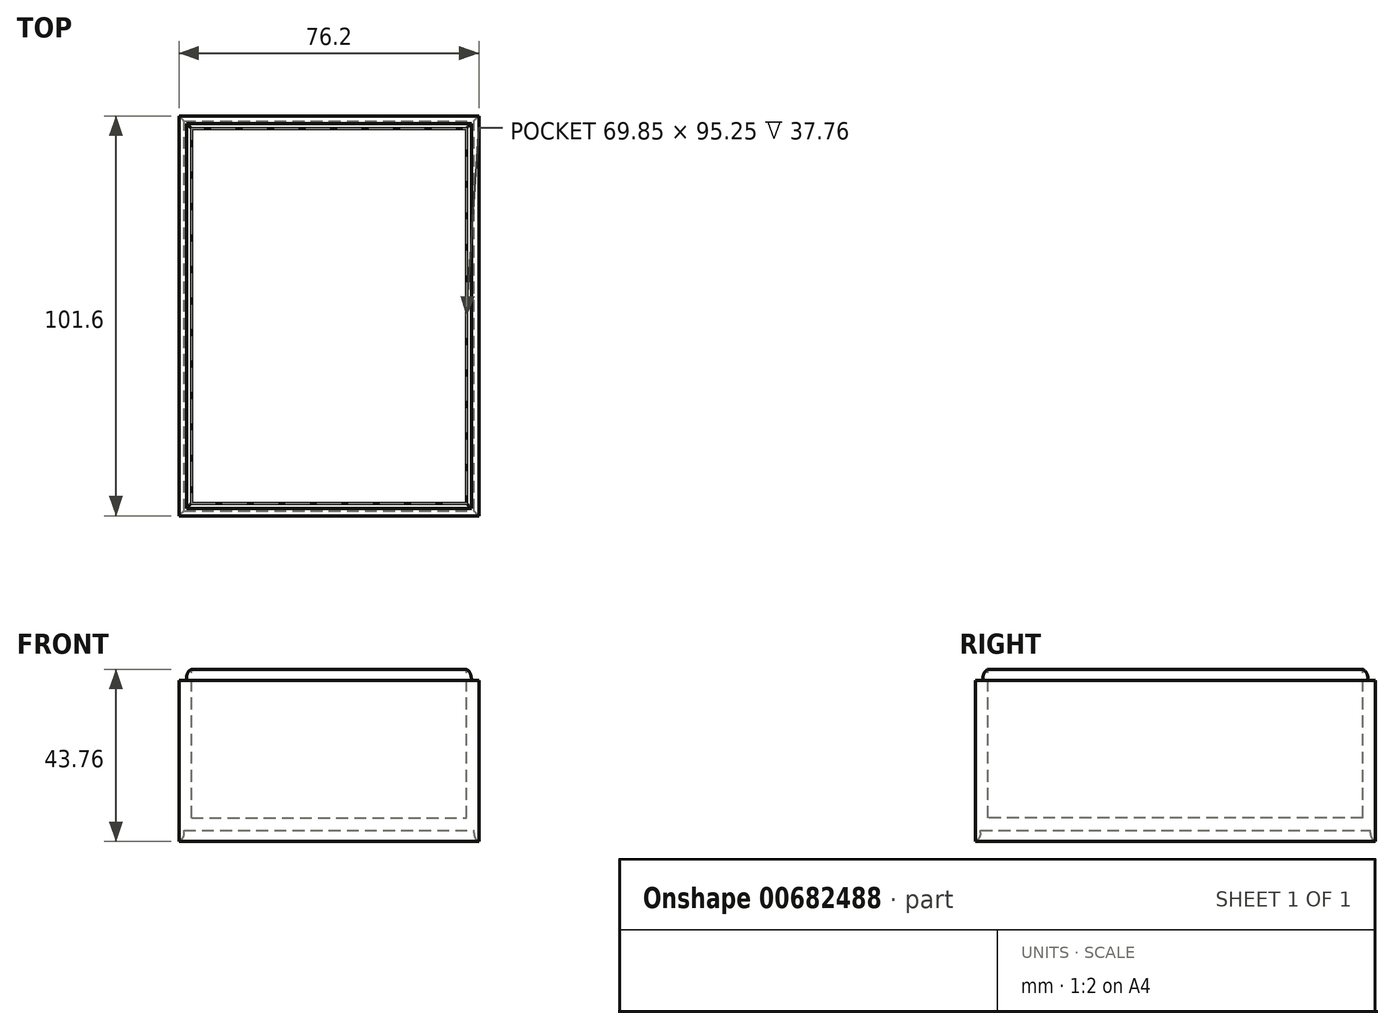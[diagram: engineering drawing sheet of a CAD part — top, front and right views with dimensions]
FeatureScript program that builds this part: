
annotation { "Feature Type Name" : "Feature", "Feature Type Description" : "" }
export const myFeature = defineFeature(function(context is Context, id is Id, definition is map)
    precondition{}
    {
        {
            var Q0;
            Q0=qCreatedBy(makeId("Top.planeOp"),FACE);
            var sketch = newSketch(context, id + "F0", { "sketchPlane" : qUnion([Q0])});
            skLineSegment(sketch, "E0.bottom", {"start": v(38.1, 50.8) * mm, "end": v(-38.1, 50.8) * mm});
            skLineSegment(sketch, "E0.top", {"start": v(38.1, -50.8) * mm, "end": v(-38.1, -50.8) * mm});
            skLineSegment(sketch, "E0.left", {"start": v(38.1, 50.8) * mm, "end": v(38.1, -50.8) * mm});
            skLineSegment(sketch, "E0.right", {"start": v(-38.1, 50.8) * mm, "end": v(-38.1, -50.8) * mm});
            skPoint(sketch, "E0.middle", {"position": v(0, 0) * mm});
            skSolve(sketch);
        }
        {
            var Q0;
            Q0 = qSketchRegion(id + "F0", true);
            extrude(context, id + "F1", {"entities" : qUnion([Q0]), "depth" : 38.1 * mm, "offsetDistance" : 25.4 * mm});
        }
        {
            var Q0;
            Q0=makeQuery(id+"F1.opExtrude","CAP_FACE",FACE,{"disambiguationData":[OSD([sQuery(id+"F0.wireOp",EDGE,"E0.bottom"),sQuery(id+"F0.wireOp",EDGE,"E0.top"),sQuery(id+"F0.wireOp",EDGE,"E0.left"),sQuery(id+"F0.wireOp",EDGE,"E0.right")])],"isStart":false});
            var sketch = newSketch(context, id + "F2", { "sketchPlane" : qUnion([Q0])});
            skLineSegment(sketch, "E1.bottom", {"start": v(-34.92, 47.63) * mm, "end": v(34.92, 47.63) * mm});
            skLineSegment(sketch, "E1.top", {"start": v(-34.92, -47.63) * mm, "end": v(34.92, -47.63) * mm});
            skLineSegment(sketch, "E1.left", {"start": v(-34.92, 47.63) * mm, "end": v(-34.92, -47.63) * mm});
            skLineSegment(sketch, "E1.right", {"start": v(34.92, 47.63) * mm, "end": v(34.92, -47.63) * mm});
            skPoint(sketch, "E1.middle", {"position": v(0, 0) * mm});
            skSolve(sketch);
        }
        {
            var Q0;
            Q0 = qSketchRegion(id + "F2", true);
            extrude(context, id + "F3", {"entities" : qUnion([Q0]), "operationType" : NewBodyOperationType.REMOVE, "oppositeDirection" : true, "depth" : 34.92 * mm, "offsetDistance" : 25.4 * mm});
        }
        {
            var Q0;
            Q0=makeQuery(id+"F1.opExtrude","CAP_FACE",FACE,{"disambiguationData":[OSD([sQuery(id+"F0.wireOp",EDGE,"E0.bottom"),sQuery(id+"F0.wireOp",EDGE,"E0.top"),sQuery(id+"F0.wireOp",EDGE,"E0.left"),sQuery(id+"F0.wireOp",EDGE,"E0.right")])],"isStart":false});
            var sketch = newSketch(context, id + "F4", { "sketchPlane" : qUnion([Q0])});
            skLineSegment(sketch, "E2.bottom", {"start": v(-36.2, 48.9) * mm, "end": v(36.2, 48.9) * mm});
            skLineSegment(sketch, "E2.top", {"start": v(-36.2, -48.9) * mm, "end": v(36.2, -48.9) * mm});
            skLineSegment(sketch, "E2.left", {"start": v(-36.2, 48.9) * mm, "end": v(-36.2, -48.9) * mm});
            skLineSegment(sketch, "E2.right", {"start": v(36.2, 48.9) * mm, "end": v(36.2, -48.9) * mm});
            skPoint(sketch, "E2.middle", {"position": v(0, 0) * mm});
            skLineSegment(sketch, "E3.bottom", {"start": v(-34.92, 47.63) * mm, "end": v(34.92, 47.63) * mm});
            skLineSegment(sketch, "E3.top", {"start": v(-34.92, -47.63) * mm, "end": v(34.92, -47.63) * mm});
            skLineSegment(sketch, "E3.left", {"start": v(-34.92, 47.63) * mm, "end": v(-34.92, -47.63) * mm});
            skLineSegment(sketch, "E3.right", {"start": v(34.92, 47.63) * mm, "end": v(34.92, -47.63) * mm});
            skSolve(sketch);
        }
        {
            var Q0;
            Q0 = qSketchRegion(id + "F4", true);
            extrude(context, id + "F5", {"entities" : qUnion([Q0]), "operationType" : NewBodyOperationType.ADD, "depth" : 3.17 * mm, "offsetDistance" : 25.4 * mm});
        }
        {
            var Q0;
            Q0=makeQuery(id+"F1.opExtrude","CAP_FACE",FACE,{"disambiguationData":[OSD([sQuery(id+"F0.wireOp",EDGE,"E0.bottom"),sQuery(id+"F0.wireOp",EDGE,"E0.top"),sQuery(id+"F0.wireOp",EDGE,"E0.left"),sQuery(id+"F0.wireOp",EDGE,"E0.right")])],"isStart":true});
            var sketch = newSketch(context, id + "F6", { "sketchPlane" : qUnion([Q0])});
            skLineSegment(sketch, "E4.bottom", {"start": v(-36.83, 49.53) * mm, "end": v(36.83, 49.53) * mm});
            skLineSegment(sketch, "E4.top", {"start": v(-36.83, -49.53) * mm, "end": v(36.83, -49.53) * mm});
            skLineSegment(sketch, "E4.left", {"start": v(-36.83, 49.53) * mm, "end": v(-36.83, -49.53) * mm});
            skLineSegment(sketch, "E4.right", {"start": v(36.83, 49.53) * mm, "end": v(36.83, -49.53) * mm});
            skPoint(sketch, "E4.middle", {"position": v(0, 0) * mm});
            skLineSegment(sketch, "E5.bottom", {"start": v(-38.1, 50.8) * mm, "end": v(38.1, 50.8) * mm});
            skLineSegment(sketch, "E5.top", {"start": v(-38.1, -50.8) * mm, "end": v(38.1, -50.8) * mm});
            skLineSegment(sketch, "E5.left", {"start": v(-38.1, 50.8) * mm, "end": v(-38.1, -50.8) * mm});
            skLineSegment(sketch, "E5.right", {"start": v(38.1, 50.8) * mm, "end": v(38.1, -50.8) * mm});
            skSolve(sketch);
        }
        {
            var Q0;
            Q0 = qSketchRegion(id + "F6", true);
            extrude(context, id + "F7", {"entities" : qUnion([Q0]), "operationType" : NewBodyOperationType.ADD, "depth" : 3.17 * mm, "offsetDistance" : 25.4 * mm});
        }
        {
            var Q0;
            Q0=makeQuery(id+"F5.opExtrude","CAP_EDGE",EDGE,{"disambiguationData":[OSD([sQuery(id+"F4.wireOp",EDGE,"E2.left")])],"isStart":false});
            var Q1;
            Q1=makeQuery(id+"F5.opExtrude","CAP_EDGE",EDGE,{"disambiguationData":[OSD([sQuery(id+"F4.wireOp",EDGE,"E2.top")])],"isStart":false});
            var Q2;
            Q2=makeQuery(id+"F5.opExtrude","CAP_EDGE",EDGE,{"disambiguationData":[OSD([sQuery(id+"F4.wireOp",EDGE,"E2.right")])],"isStart":false});
            var Q3;
            Q3=makeQuery(id+"F5.opExtrude","CAP_EDGE",EDGE,{"disambiguationData":[OSD([sQuery(id+"F4.wireOp",EDGE,"E2.bottom")])],"isStart":false});
            var Q4;
            Q4=makeQuery(id+"F7.opExtrude","CAP_EDGE",EDGE,{"disambiguationData":[OSD([sQuery(id+"F6.wireOp",EDGE,"E4.left")])],"isStart":false});
            var Q5;
            Q5=makeQuery(id+"F7.opExtrude","CAP_EDGE",EDGE,{"disambiguationData":[OSD([sQuery(id+"F6.wireOp",EDGE,"E4.bottom")])],"isStart":false});
            var Q6;
            Q6=makeQuery(id+"F7.opExtrude","CAP_EDGE",EDGE,{"disambiguationData":[OSD([sQuery(id+"F6.wireOp",EDGE,"E4.right")])],"isStart":false});
            var Q7;
            Q7=makeQuery(id+"F7.opExtrude","CAP_EDGE",EDGE,{"disambiguationData":[OSD([sQuery(id+"F6.wireOp",EDGE,"E4.top")])],"isStart":false});
            fillet(context, id + "F8", {"entities" : qUnion([Q0, Q1, Q2, Q3, Q4, Q5, Q6, Q7]), "radius" : 2.54 * mm, "tangentPropagation" : true, "allowEdgeOverflow" : false});
        }
    });
